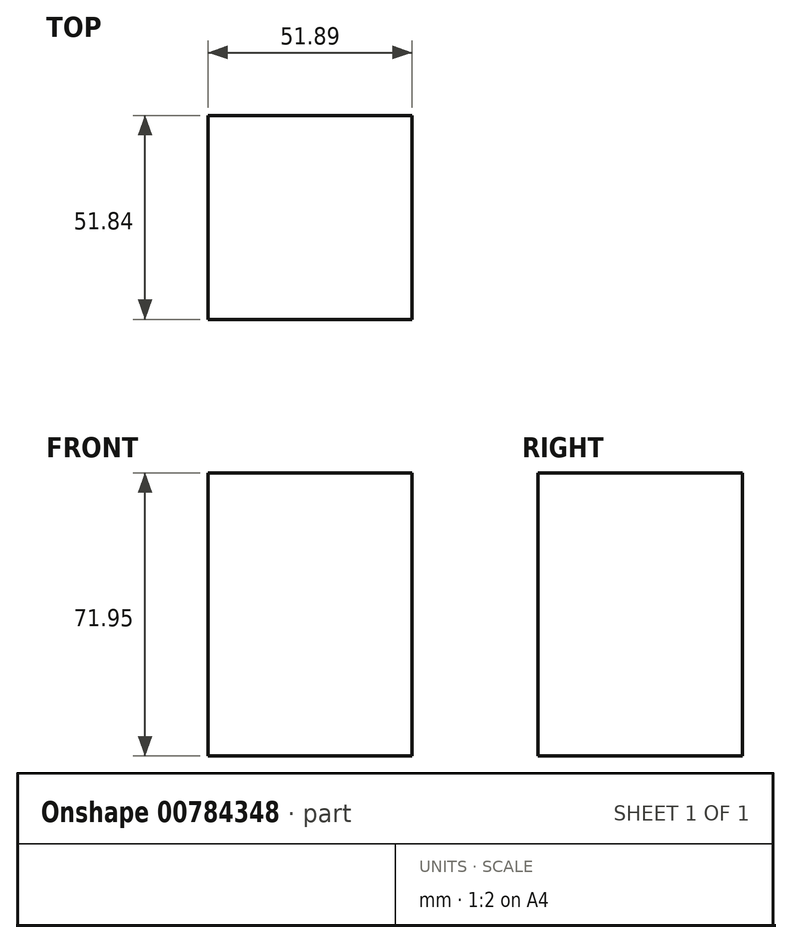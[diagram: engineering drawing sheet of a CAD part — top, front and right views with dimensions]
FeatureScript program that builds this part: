
annotation { "Feature Type Name" : "Feature", "Feature Type Description" : "" }
export const myFeature = defineFeature(function(context is Context, id is Id, definition is map)
    precondition{}
    {
        {
            var Q0;
            Q0=qCreatedBy(makeId("Top.planeOp"),FACE);
            var sketch = newSketch(context, id + "F0", { "sketchPlane" : qUnion([Q0])});
            skLineSegment(sketch, "E0.bottom", {"start": v(26.07, -22.45) * mm, "end": v(-25.82, -22.45) * mm});
            skLineSegment(sketch, "E0.top", {"start": v(26.07, 29.4) * mm, "end": v(-25.82, 29.4) * mm});
            skLineSegment(sketch, "E0.left", {"start": v(26.07, -22.45) * mm, "end": v(26.07, 29.4) * mm});
            skLineSegment(sketch, "E0.right", {"start": v(-25.82, -22.45) * mm, "end": v(-25.82, 29.4) * mm});
            skSolve(sketch);
        }
        {
            var Q0;
            Q0=makeQuery(id+"F0.imprint","IMPRINT",FACE,{"disambiguationData":[TD([[makeQuery(id+"F0.imprint","IMPRINT",EDGE,{"derivedFrom":sQuery(id+"F0.wireOp",EDGE,"E0.bottom")}),-1.0]])]});
            var Q1;
            Q1 = qSketchRegion(id + "F0", true);
            extrude(context, id + "F1", {"entities" : qUnion([Q0, Q1]), "depth" : 71.95 * mm, "offsetDistance" : 25.4 * mm});
        }
    });
